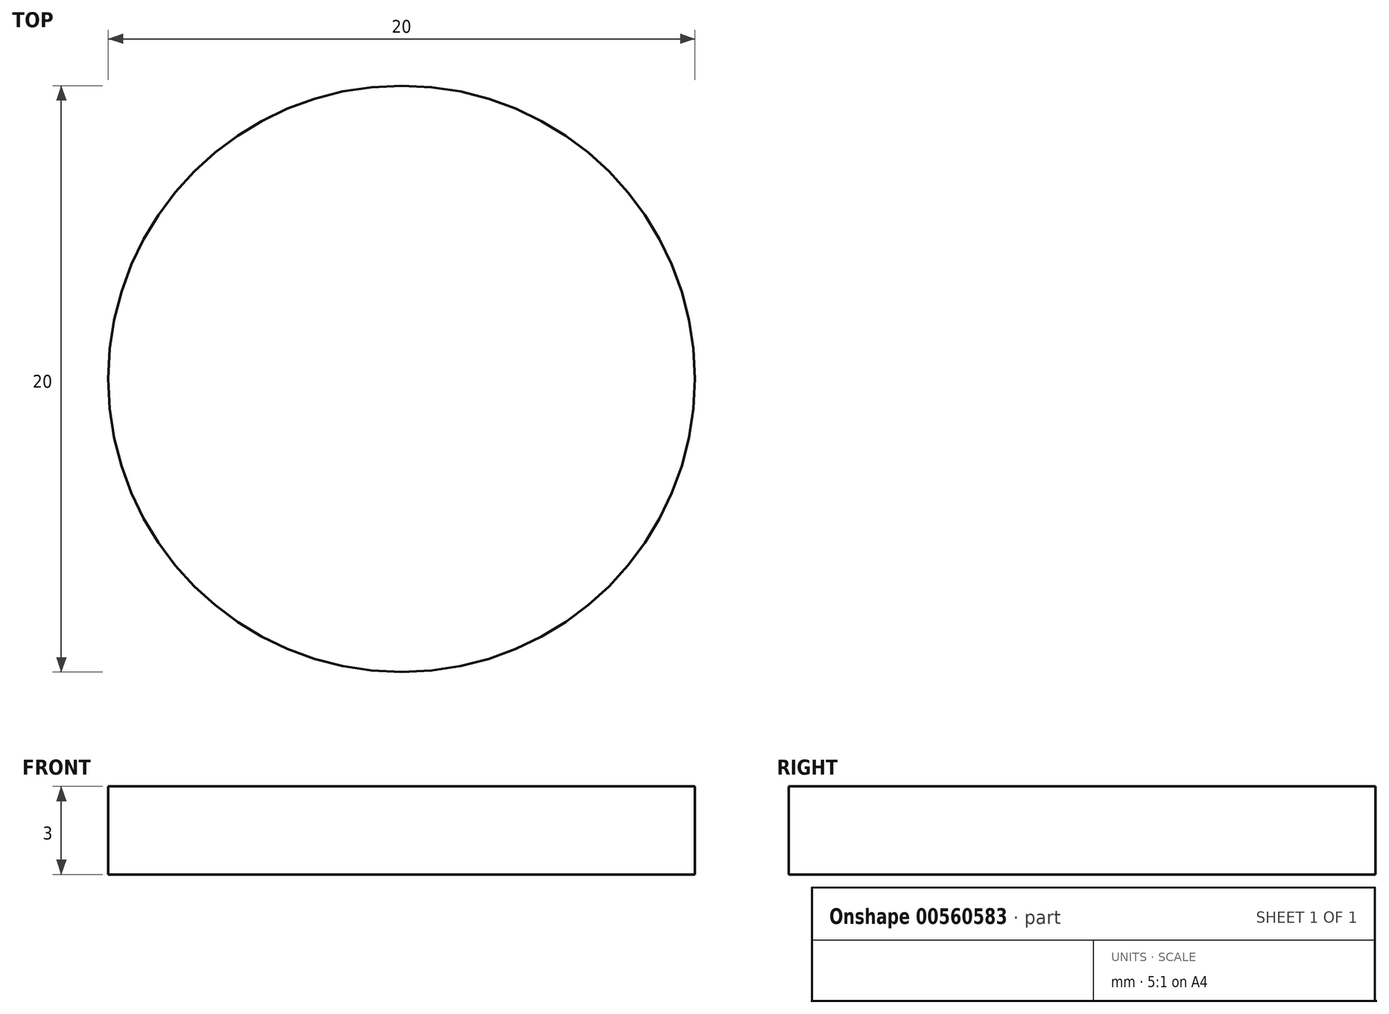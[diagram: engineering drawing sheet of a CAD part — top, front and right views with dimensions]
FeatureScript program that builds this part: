
annotation { "Feature Type Name" : "Feature", "Feature Type Description" : "" }
export const myFeature = defineFeature(function(context is Context, id is Id, definition is map)
    precondition{}
    {
        {
            var Q0;
            Q0=qCreatedBy(makeId("Top.planeOp"),FACE);
            var sketch = newSketch(context, id + "F0", { "sketchPlane" : qUnion([Q0])});
            skCircle(sketch, "E0", {"center": v(0, 0) * mm, "radius": 10 * mm});
            skSolve(sketch);
        }
        {
            var Q0;
            Q0 = qSketchRegion(id + "F0", true);
            extrude(context, id + "F1", {"entities" : qUnion([Q0]), "depth" : 3 * mm, "offsetDistance" : 25 * mm});
        }
    });
